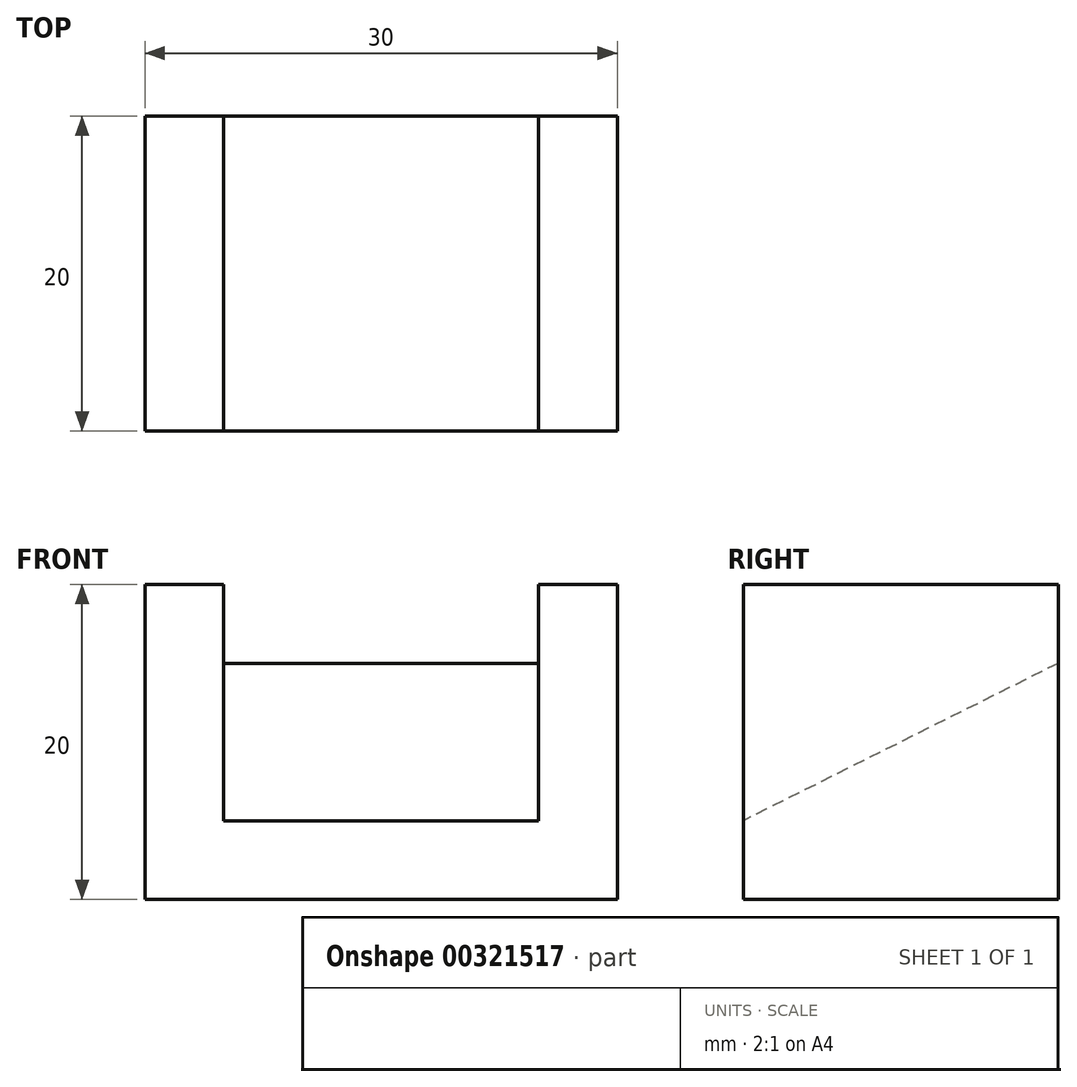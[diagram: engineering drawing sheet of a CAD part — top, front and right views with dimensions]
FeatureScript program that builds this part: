
annotation { "Feature Type Name" : "Feature", "Feature Type Description" : "" }
export const myFeature = defineFeature(function(context is Context, id is Id, definition is map)
    precondition{}
    {
        {
            var Q0;
            Q0=qCreatedBy(makeId("Right.planeOp"),FACE);
            var sketch = newSketch(context, id + "F0", { "sketchPlane" : qUnion([Q0])});
            skLineSegment(sketch, "E0.bottom", {"start": v(0, 0) * mm, "end": v(20, 0) * mm});
            skLineSegment(sketch, "E0.top", {"start": v(0, 20) * mm, "end": v(20, 20) * mm});
            skLineSegment(sketch, "E0.left", {"start": v(0, 0) * mm, "end": v(0, 20) * mm});
            skLineSegment(sketch, "E0.right", {"start": v(20, 0) * mm, "end": v(20, 20) * mm});
            skSolve(sketch);
        }
        {
            var Q0;
            Q0=makeQuery(id+"F0.imprint","IMPRINT",FACE,{"disambiguationData":[TD([[makeQuery(id+"F0.imprint","IMPRINT",EDGE,{"derivedFrom":sQuery(id+"F0.wireOp",EDGE,"E0.bottom")}),1.0]])]});
            extrude(context, id + "F1", {"entities" : qUnion([Q0]), "depth" : 5 * mm});
        }
        {
            var Q0;
            Q0=makeQuery(id+"F1.opExtrude","CAP_FACE",FACE,{"disambiguationData":[OSD([sQuery(id+"F0.wireOp",EDGE,"E0.bottom"),sQuery(id+"F0.wireOp",EDGE,"E0.top"),sQuery(id+"F0.wireOp",EDGE,"E0.left"),sQuery(id+"F0.wireOp",EDGE,"E0.right")])],"isStart":false});
            var sketch = newSketch(context, id + "F2", { "sketchPlane" : qUnion([Q0])});
            skLineSegment(sketch, "E1", {"start": v(0, 0) * mm, "end": v(0, 5) * mm});
            skLineSegment(sketch, "E2", {"start": v(20, 15) * mm, "end": v(0, 5) * mm});
            skLineSegment(sketch, "E3", {"start": v(0, 0) * mm, "end": v(20, 0) * mm});
            skLineSegment(sketch, "E4", {"start": v(20, 0) * mm, "end": v(20, 15) * mm});
            skSolve(sketch);
        }
        {
            var Q0;
            Q0 = qSketchRegion(id + "F2", true);
            extrude(context, id + "F3", {"entities" : qUnion([Q0]), "operationType" : NewBodyOperationType.ADD, "depth" : 20 * mm});
        }
        {
            var Q0;
            Q0=makeQuery(id+"F3.opExtrude","CAP_FACE",FACE,{"disambiguationData":[OSD([sQuery(id+"F2.wireOp",EDGE,"E1"),sQuery(id+"F2.wireOp",EDGE,"E2"),sQuery(id+"F2.wireOp",EDGE,"E3"),sQuery(id+"F2.wireOp",EDGE,"E4")])],"isStart":false});
            var sketch = newSketch(context, id + "F4", { "sketchPlane" : qUnion([Q0])});
            skLineSegment(sketch, "E5.bottom", {"start": v(0, 0) * mm, "end": v(20, 0) * mm});
            skLineSegment(sketch, "E5.top", {"start": v(0, 20) * mm, "end": v(20, 20) * mm});
            skLineSegment(sketch, "E5.left", {"start": v(0, 0) * mm, "end": v(0, 20) * mm});
            skLineSegment(sketch, "E5.right", {"start": v(20, 0) * mm, "end": v(20, 20) * mm});
            skSolve(sketch);
        }
        {
            var Q0;
            Q0 = qSketchRegion(id + "F4", true);
            extrude(context, id + "F5", {"entities" : qUnion([Q0]), "operationType" : NewBodyOperationType.ADD, "depth" : 5 * mm});
        }
    });
